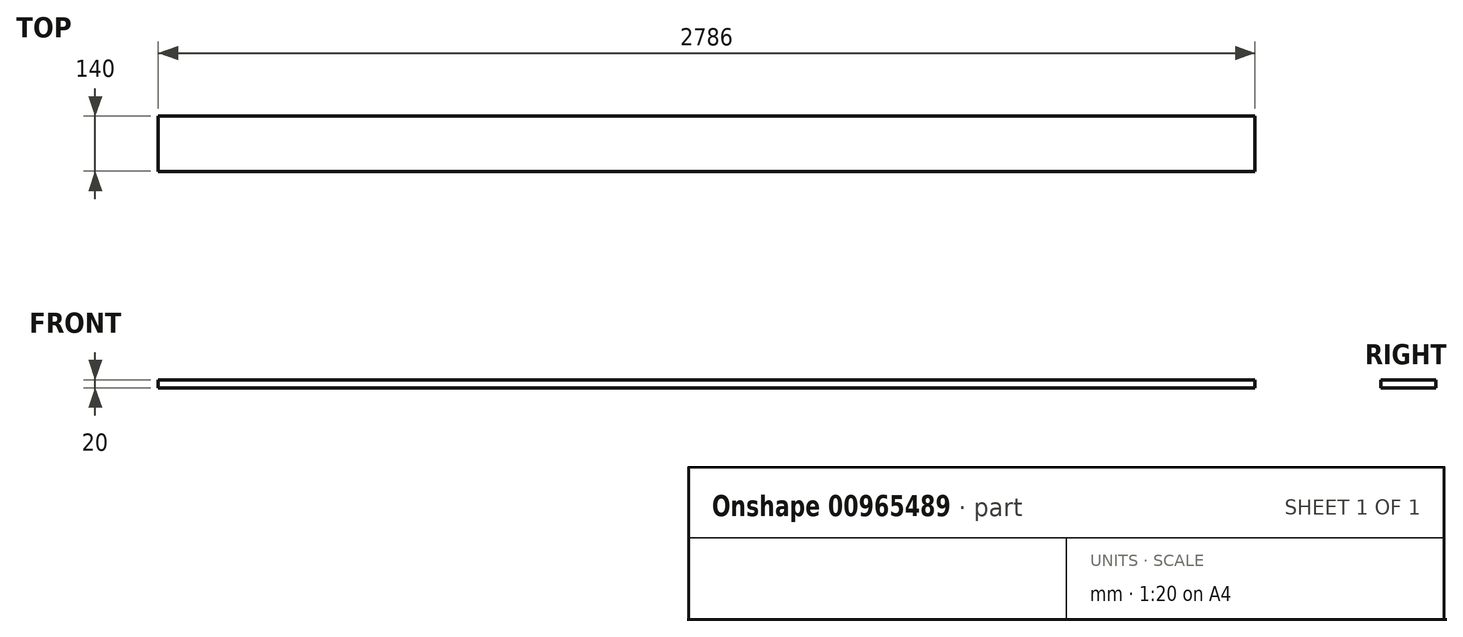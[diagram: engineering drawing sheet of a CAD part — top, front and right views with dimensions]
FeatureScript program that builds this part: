
annotation { "Feature Type Name" : "Feature", "Feature Type Description" : "" }
export const myFeature = defineFeature(function(context is Context, id is Id, definition is map)
    precondition{}
    {
        {
            var Q0;
            Q0=qCreatedBy(makeId("Top.planeOp"),FACE);
            var sketch = newSketch(context, id + "F0", { "sketchPlane" : qUnion([Q0])});
            skLineSegment(sketch, "E0.bottom", {"start": v(-378.74, 64.08) * mm, "end": v(2407.26, 64.08) * mm});
            skLineSegment(sketch, "E0.top", {"start": v(-378.74, -75.92) * mm, "end": v(2407.26, -75.92) * mm});
            skLineSegment(sketch, "E0.left", {"start": v(-378.74, 64.08) * mm, "end": v(-378.74, -75.92) * mm});
            skLineSegment(sketch, "E0.right", {"start": v(2407.26, 64.08) * mm, "end": v(2407.26, -75.92) * mm});
            skSolve(sketch);
        }
        {
            var Q0;
            Q0=makeQuery(id+"F0.imprint","IMPRINT",FACE,{"disambiguationData":[TD([[makeQuery(id+"F0.imprint","IMPRINT",EDGE,{"derivedFrom":sQuery(id+"F0.wireOp",EDGE,"E0.bottom")}),-1.0]])]});
            extrude(context, id + "F1", {"entities" : qUnion([Q0]), "depth" : 20 * mm, "offsetDistance" : 25 * mm});
        }
    });
